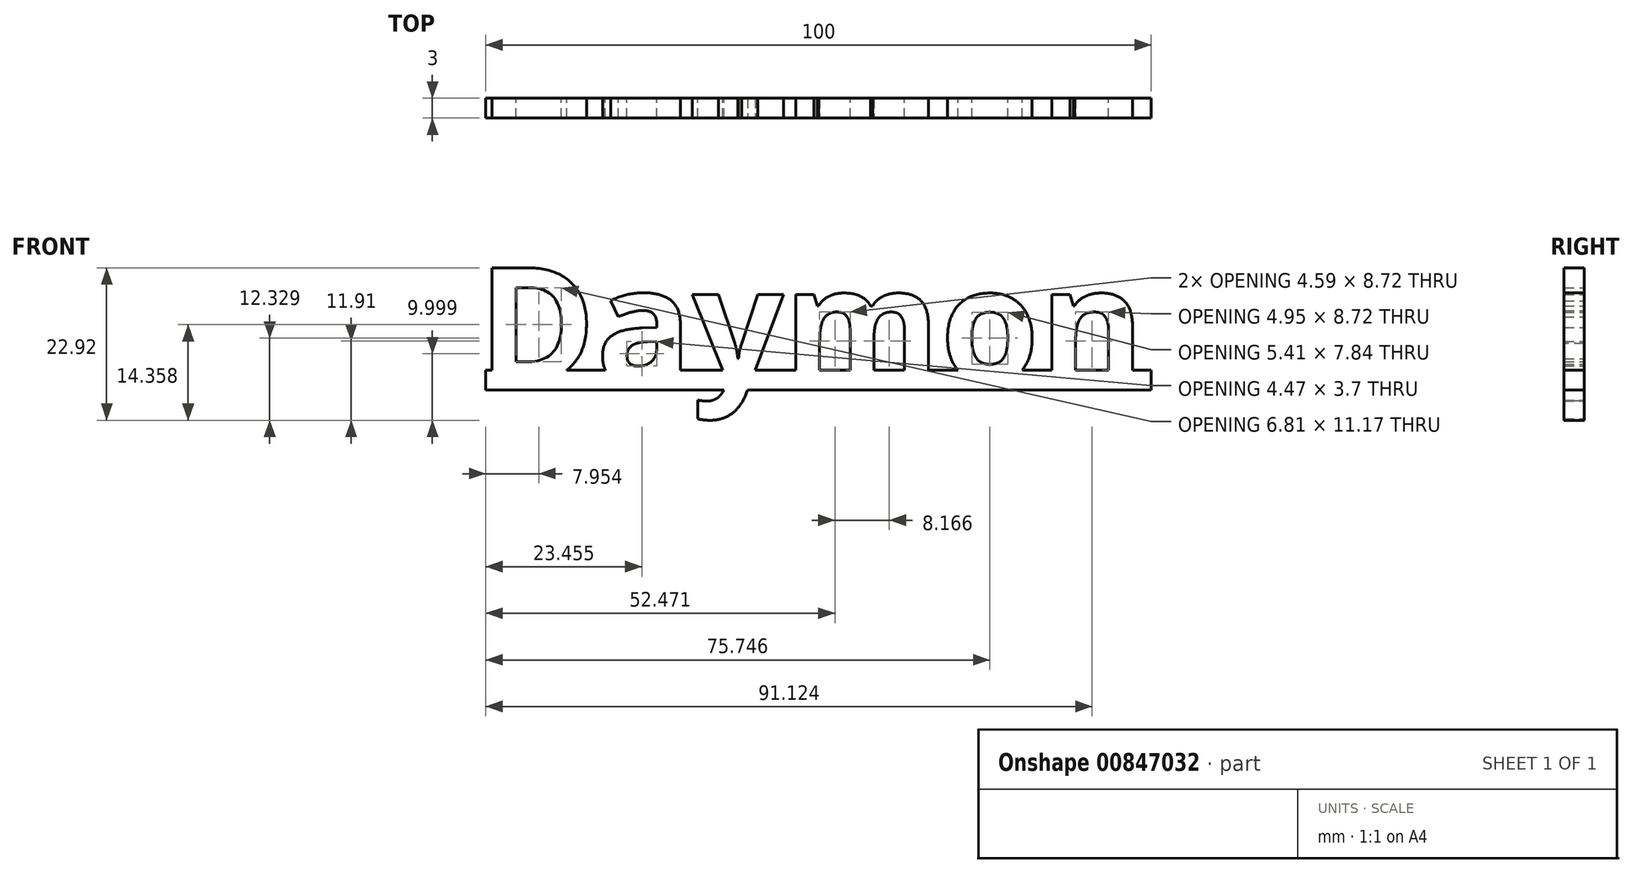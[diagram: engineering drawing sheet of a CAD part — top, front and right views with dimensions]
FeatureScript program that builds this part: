
annotation { "Feature Type Name" : "Feature", "Feature Type Description" : "" }
export const myFeature = defineFeature(function(context is Context, id is Id, definition is map)
    precondition{}
    {
        {
            var Q0;
            Q0=qCreatedBy(makeId("Front.planeOp"),FACE);
            var sketch = newSketch(context, id + "F0", { "sketchPlane" : qUnion([Q0])});
            skText(sketch, "E0", { "text": "Daymon", "fontName": "OpenSans-Bold.ttf"});
            const initialGuessF0  = {"E0": [-0.05088, 0.00043, 1, 0, 0.0173]};
            skSetInitialGuess(sketch, initialGuessF0);
            skSolve(sketch);
        }
        {
            var Q0;
            Q0 = qSketchRegion(id + "F0", true);
            extrude(context, id + "F1", {"entities" : qUnion([Q0]), "depth" : 3 * mm, "offsetDistance" : 25 * mm});
        }
        {
            var Q0;
            Q0=qCreatedBy(makeId("Front.planeOp"),FACE);
            var sketch = newSketch(context, id + "F2", { "sketchPlane" : qUnion([Q0])});
            skLineSegment(sketch, "E1.bottom", {"start": v(-49.63, 2.21) * mm, "end": v(50.37, 2.21) * mm});
            skLineSegment(sketch, "E1.top", {"start": v(-49.63, -0.79) * mm, "end": v(50.37, -0.79) * mm});
            skLineSegment(sketch, "E1.left", {"start": v(-49.63, 2.21) * mm, "end": v(-49.63, -0.79) * mm});
            skLineSegment(sketch, "E1.right", {"start": v(50.37, 2.21) * mm, "end": v(50.37, -0.79) * mm});
            skSolve(sketch);
        }
        {
            var Q0;
            Q0 = qSketchRegion(id + "F2", true);
            extrude(context, id + "F3", {"entities" : qUnion([Q0]), "operationType" : NewBodyOperationType.ADD, "depth" : 3 * mm, "offsetDistance" : 25 * mm});
        }
        {
            var Q0;
            Q0 = qSketchRegion(id + "F2", true);
            extrude(context, id + "F4", {"entities" : qUnion([Q0]), "operationType" : NewBodyOperationType.ADD, "depth" : 3 * mm, "offsetDistance" : 25 * mm});
        }
    });
